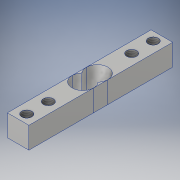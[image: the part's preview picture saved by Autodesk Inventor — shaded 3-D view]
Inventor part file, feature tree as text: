
AUTODESK INVENTOR PART (.ipt)
format: ipt  version: 2019 (Build 230136000, 136)  size: 143,872 bytes
history: native  units: mm
features: thread x4, extrude x2, sketch x2
ambient origin geometry x8: Origin, YZ Plane, XZ Plane, XY Plane, X Axis, Y Axis, Z Axis, Center Point
bodies: Solid1 (feature_tree)
feature tree (8):
  extrude  "Extrusion1"  Depth=15.0mm
  extrude  "Extrusion2"  Depth=15.0mm
  thread  "Thread1"  [1 undecoded]
  thread  "Thread2"  [1 undecoded]
  thread  "Thread3"  [1 undecoded]
  thread  "Thread4"  [1 undecoded]
  sketch  "Sketch2"  dims[d0=15.0mm d1=15.0mm]
  sketch  "Sketch3"  dims[d2=10.0mm d3=15.0mm d4=7.5mm d5=100.0mm d6=50.0mm d7=55.0mm d8=15.0mm d9=0.0mm d10=7.0mm d11=7.0mm d12=15.0mm d13=7.5mm d14=6.0mm d15=21.0mm d16=7.0mm d17=7.0mm d18=15.0mm d19=6.0mm d20=7.5mm d21=21.0mm d22=15.0mm d23=0.0mm d24=10.0mm d25=0.0mm d26=10.0mm d27=0.0mm d28=10.0mm d29=0.0mm d30=10.0mm d31=0.0mm]
note: 4 required parameter values undecoded (feature->parameter linkage not recoverable at this tier; creation-order binding heuristic only, values carry confidence <= 0.55)
